# Revit family: 0010317
name_source: partatom
category: Lighting Fixtures
revit_build: Autodesk Revit 2018 (Build: 20170223_1515(x64)
units: mm (PartAtom-declared; Revit-internal decimal feet)

## family parameters
Cut with Voids When Loaded = No
Host = Face
Light Source = Yes
OmniClass Number = 23.80.70.00
OmniClass Title = Lighting
Part Type = Normal
Room Calculation Point = No
Round Connector Dimension = Use Diameter
Shared = No

## types (1)
- 0010317 RESISTO GRP 1500 IP66 7000LM 840
    Apparent Load = 51 VA
    Assembly Code = D5020200
    AssetType = Fixed
    ClassificationName = Uniclass2015
    ClassificationValue = EF_70_80
    Color Filter = 16777215
    Cost = 0 $
    Default Elevation = 1219 mm
    Description = Resisto GRP, integrated LED weatherproof luminaire, with smooth body finish optimized for LEDs with flat diffuser, easy to handle. Stainless steel diffuser clips and fixing brackets for surface mounting. The luminaire benefits from a water and dust resistant GRP body and PMMA diffuser. 7000lm; 51W; 137lm/W; 4000K; SDCM<4; non dimmable;  CRI80; IP66; IK02; Class I; 72,000hrs (L80B20) lifespan;  1454mm x 90mm x 120mm; D-mark.
    Dimming Lamp Color Temperature Shift = <None>
    DocumentationLiterature = http://www.sylvania-lighting.com
    ElectricShockClassification = 137
    IfcExportAs = Class I
    IfcExportType = IfcLightFixtureType
    ImpactProtectionIndex = IfcLightFixtureType
    IngressProtection = IfcLightFixtureType
    InputNominalFrequency = 4000
    InputVoltage = 0
    LampColourRenderingIndex = 16500
    LampColourTemperature = LED
    LampMacAdamStep = 80
    LampNominalLuminous = 4000 K
    LightOutputRatio = LED
    LuminaireType = 0
    ManufacturerName = 137 lm/W
    Material = Feilo Sylvania
    Material_1_SYL = <By Category>
    Material_2_SYL = <By Category>
    Material_3_SYL = <By Category>
    Material_4_SYL = <By Category>
    Model = Resisto GRP 1500 IP66 7000lm 840
    ModelNumber = 0010317
    ModelReference = Resisto GRP 1500 IP66 7000lm 840
    Name = Resisto GRP 1500 IP66 7000lm 840
    NominalDepth = 100 mm  [stored 0.328084 ft]
    NominalHeight = 90 mm  [stored 0.295276 ft]
    NominalLength = 1450 mm  [stored 4.75722 ft]
    Photometric Web File = 0010317.ies
    PowerConsumption = Lighting
    PowerFactor = 0
    Tilt Angle = 60.00°
    Type Image = <None>
    TypeName = Resisto GRP 1500 IP66 7000lm 840
    URL = 1
    Voltage = 0 V
    WarrantyDescription = http://www.sylvania-lighting.com

note: [stored X ft] marks values corroborated as IEEE doubles in the binary element streams (Revit-internal decimal feet)

## geometry (parser evidence)
native form markers: Sweep x3
no freeform markers — native parametric forms only
